# Revit family: HL_RU_Anti-flooding valve_HL720.0-A-171212
name_source: partatom
category: Příslušenství trubek
units: mm (PartAtom-declared; Revit-internal decimal feet)

## family parameters
Kóta kulaté spojky = Použít průměr
Nadpis OmniClass = Non-Return Valves for Liquid Services
Ořezat dutým tvarem při načtení = Ne
Sdílené = Ne
Typ dílu = Zakončení
Vždy vertikální = Ano
Založené na pracovní rovině = Ne
Číslo OmniClass = 23.65.55.14.21

## types (1)
- HL_Затвор_HL720.0
    Cena = 0 $
    EAN = 9003076172009
    Indexovaná poznámka = HL720.0
    Komentáře k typům = Затвор DN200 с заслонкой из нержавеющей стали и муфтой для труб из синтетического материала.
    Model = HL720.0
    Popis = Механический канализационный затвор
    URL = http://www.hutterer-lechner.com
    Výchozí výška = 0 mm  [stored 0 ft]
    Výrobce = HL Hutterer & Lechner GmbH
    ВЕС = 1,56 kg
    ВЫСОТА МОНТАЖА = 246 mm
    МАТЕРИАЛ = ABS
    НОМИНАЛЬНЫЙ ДИАМЕТР = 200 mm
    РАЗМЕР = DN200

note: [stored X ft] marks values corroborated as IEEE doubles in the binary element streams (Revit-internal decimal feet)
